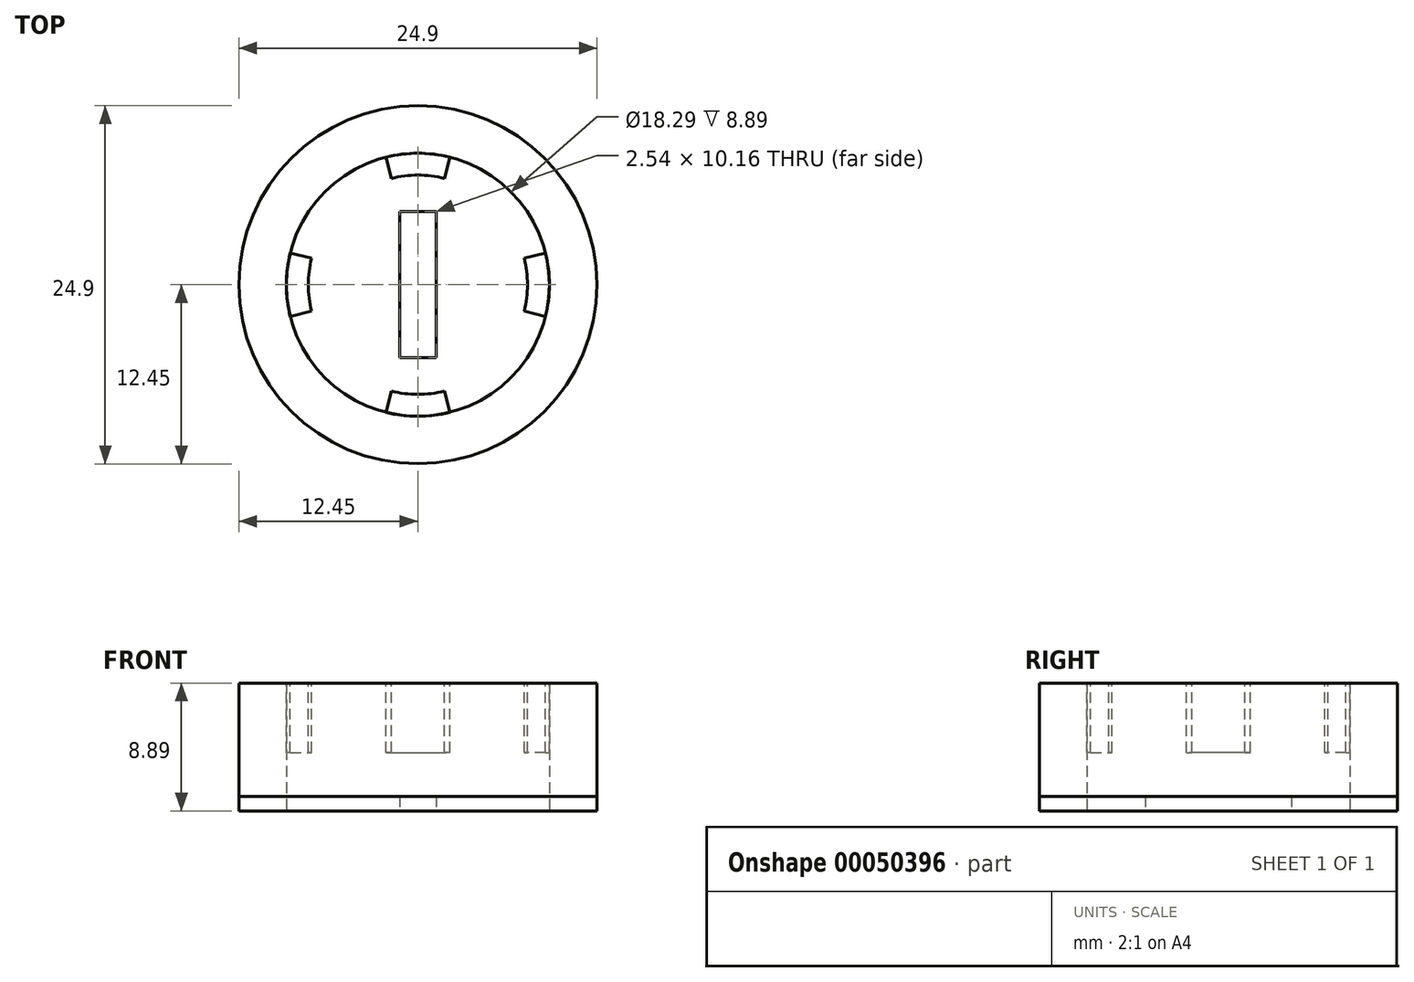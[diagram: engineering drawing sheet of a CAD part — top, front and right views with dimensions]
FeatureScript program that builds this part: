
annotation { "Feature Type Name" : "Feature", "Feature Type Description" : "" }
export const myFeature = defineFeature(function(context is Context, id is Id, definition is map)
    precondition{}
    {
        {
            var Q0;
            Q0=qCreatedBy(makeId("Top.planeOp"),FACE);
            var sketch = newSketch(context, id + "F0", { "sketchPlane" : qUnion([Q0])});
            skCircle(sketch, "E0", {"center": v(0, 0) * mm, "radius": 7.62 * mm});
            skCircle(sketch, "E1", {"center": v(0, 0) * mm, "radius": 12.45 * mm});
            skCircle(sketch, "E2", {"center": v(0, 0) * mm, "radius": 9.14 * mm});
            skLineSegment(sketch, "E3", {"start": v(0, 0) * mm, "end": v(0, 9.14) * mm});
            skLineSegment(sketch, "E4.1.0", {"start": v(0, 0) * mm, "end": v(-2.37, 8.83) * mm});
            skLineSegment(sketch, "E4.2.0", {"start": v(0, 0) * mm, "end": v(-4.57, 7.92) * mm});
            skLineSegment(sketch, "E4.3.0", {"start": v(0, 0) * mm, "end": v(-6.47, 6.47) * mm});
            skLineSegment(sketch, "E4.4.0", {"start": v(0, 0) * mm, "end": v(-7.92, 4.57) * mm});
            skLineSegment(sketch, "E4.5.0", {"start": v(0, 0) * mm, "end": v(-8.83, 2.37) * mm});
            skLineSegment(sketch, "E4.6.0", {"start": v(0, 0) * mm, "end": v(-9.14, 0) * mm});
            skLineSegment(sketch, "E4.7.0", {"start": v(0, 0) * mm, "end": v(-8.83, -2.37) * mm});
            skLineSegment(sketch, "E4.8.0", {"start": v(0, 0) * mm, "end": v(-7.92, -4.57) * mm});
            skLineSegment(sketch, "E4.9.0", {"start": v(0, 0) * mm, "end": v(-6.47, -6.47) * mm});
            skLineSegment(sketch, "E4.10.0", {"start": v(0, 0) * mm, "end": v(-4.57, -7.92) * mm});
            skLineSegment(sketch, "E4.11.0", {"start": v(0, 0) * mm, "end": v(-2.37, -8.83) * mm});
            skLineSegment(sketch, "E4.12.0", {"start": v(0, 0) * mm, "end": v(0, -9.14) * mm});
            skLineSegment(sketch, "E4.13.0", {"start": v(0, 0) * mm, "end": v(2.37, -8.83) * mm});
            skLineSegment(sketch, "E4.14.0", {"start": v(0, 0) * mm, "end": v(4.57, -7.92) * mm});
            skLineSegment(sketch, "E4.15.0", {"start": v(0, 0) * mm, "end": v(6.47, -6.47) * mm});
            skLineSegment(sketch, "E4.16.0", {"start": v(0, 0) * mm, "end": v(7.92, -4.57) * mm});
            skLineSegment(sketch, "E4.17.0", {"start": v(0, 0) * mm, "end": v(8.83, -2.37) * mm});
            skLineSegment(sketch, "E4.18.0", {"start": v(0, 0) * mm, "end": v(9.14, 0) * mm});
            skLineSegment(sketch, "E4.19.0", {"start": v(0, 0) * mm, "end": v(8.83, 2.37) * mm});
            skLineSegment(sketch, "E4.20.0", {"start": v(0, 0) * mm, "end": v(7.92, 4.57) * mm});
            skLineSegment(sketch, "E4.21.0", {"start": v(0, 0) * mm, "end": v(6.47, 6.47) * mm});
            skLineSegment(sketch, "E4.22.0", {"start": v(0, 0) * mm, "end": v(4.57, 7.92) * mm});
            skLineSegment(sketch, "E4.23.0", {"start": v(0, 0) * mm, "end": v(2.37, 8.83) * mm});
            skLineSegment(sketch, "E5", {"start": v(0, 0) * mm, "end": v(2.21, 8.87) * mm});
            skLineSegment(sketch, "E6", {"start": v(0, 0) * mm, "end": v(-2.21, 8.87) * mm});
            skLineSegment(sketch, "E7.1.0", {"start": v(0, 0) * mm, "end": v(-8.87, -2.21) * mm});
            skLineSegment(sketch, "E7.1.1", {"start": v(0, 0) * mm, "end": v(-8.87, 2.21) * mm});
            skLineSegment(sketch, "E7.2.0", {"start": v(0, 0) * mm, "end": v(2.21, -8.87) * mm});
            skLineSegment(sketch, "E7.2.1", {"start": v(0, 0) * mm, "end": v(-2.21, -8.87) * mm});
            skLineSegment(sketch, "E7.3.0", {"start": v(0, 0) * mm, "end": v(8.87, 2.21) * mm});
            skLineSegment(sketch, "E7.3.1", {"start": v(0, 0) * mm, "end": v(8.87, -2.21) * mm});
            skSolve(sketch);
        }
        {
            var Q0;
            Q0=makeQuery(id+"F0.imprint","IMPRINT",FACE,{"disambiguationData":[TD([[makeQuery(id+"F0.imprint","IMPRINT",EDGE,{"derivedFrom":sQuery(id+"F0.wireOp",EDGE,"E1")}),1.0]])]});
            extrude(context, id + "F1", {"entities" : qUnion([Q0]), "depth" : 8.9 * mm});
        }
        {
            var Q0;
            Q0=makeQuery(id+"F1.opExtrude","CAP_FACE",FACE,{"disambiguationData":[OSD([sQuery(id+"F0.wireOp",EDGE,"E1"),sQuery(id+"F0.wireOp",EDGE,"E2")])],"isStart":false});
            var sketch = newSketch(context, id + "F2", { "sketchPlane" : qUnion([Q0])});
            skLineSegment(sketch, "E8.0.0", {"start": v(-9.14, 0) * mm, "end": v(-7.62, 0) * mm});
            skArc(sketch, "E8.0.1", {"start": v(-7.62, 0) * mm, "mid": v(-7.56, 0.93) * mm, "end": v(-7.4, 1.84) * mm});
            skLineSegment(sketch, "E8.0.2", {"start": v(-7.4, 1.84) * mm, "end": v(-8.87, 2.21) * mm});
            skArc(sketch, "E8.0.3", {"start": v(-8.87, 2.21) * mm, "mid": v(-9.08, 1.11) * mm, "end": v(-9.14, 0) * mm});
            skArc(sketch, "E9.0.0", {"start": v(-7.4, -1.84) * mm, "mid": v(-7.56, -0.93) * mm, "end": v(-7.62, 0) * mm});
            skLineSegment(sketch, "E9.0.1", {"start": v(-7.62, 0) * mm, "end": v(-9.14, 0) * mm});
            skArc(sketch, "E9.0.2", {"start": v(-9.14, 0) * mm, "mid": v(-9.08, -1.11) * mm, "end": v(-8.87, -2.21) * mm});
            skLineSegment(sketch, "E9.0.3", {"start": v(-8.87, -2.21) * mm, "end": v(-7.4, -1.84) * mm});
            skLineSegment(sketch, "E10.0.0", {"start": v(0, -9.14) * mm, "end": v(0, -7.62) * mm});
            skArc(sketch, "E10.0.1", {"start": v(0, -7.62) * mm, "mid": v(-0.93, -7.56) * mm, "end": v(-1.84, -7.4) * mm});
            skLineSegment(sketch, "E10.0.2", {"start": v(-1.84, -7.4) * mm, "end": v(-2.21, -8.87) * mm});
            skArc(sketch, "E10.0.3", {"start": v(-2.21, -8.87) * mm, "mid": v(-1.11, -9.08) * mm, "end": v(0, -9.14) * mm});
            skArc(sketch, "E11.0.0", {"start": v(1.84, -7.4) * mm, "mid": v(0.93, -7.56) * mm, "end": v(0, -7.62) * mm});
            skLineSegment(sketch, "E11.0.1", {"start": v(0, -7.62) * mm, "end": v(0, -9.14) * mm});
            skArc(sketch, "E11.0.2", {"start": v(0, -9.14) * mm, "mid": v(1.11, -9.08) * mm, "end": v(2.21, -8.87) * mm});
            skLineSegment(sketch, "E11.0.3", {"start": v(2.21, -8.87) * mm, "end": v(1.84, -7.4) * mm});
            skLineSegment(sketch, "E12.0.0", {"start": v(9.14, 0) * mm, "end": v(7.62, 0) * mm});
            skArc(sketch, "E12.0.1", {"start": v(7.62, 0) * mm, "mid": v(7.56, -0.93) * mm, "end": v(7.4, -1.84) * mm});
            skLineSegment(sketch, "E12.0.2", {"start": v(7.4, -1.84) * mm, "end": v(8.87, -2.21) * mm});
            skArc(sketch, "E12.0.3", {"start": v(8.87, -2.21) * mm, "mid": v(9.08, -1.11) * mm, "end": v(9.14, 0) * mm});
            skArc(sketch, "E13.0.0", {"start": v(7.4, 1.84) * mm, "mid": v(7.56, 0.93) * mm, "end": v(7.62, 0) * mm});
            skLineSegment(sketch, "E13.0.1", {"start": v(7.62, 0) * mm, "end": v(9.14, 0) * mm});
            skArc(sketch, "E13.0.2", {"start": v(9.14, 0) * mm, "mid": v(9.08, 1.11) * mm, "end": v(8.87, 2.21) * mm});
            skLineSegment(sketch, "E13.0.3", {"start": v(8.87, 2.21) * mm, "end": v(7.4, 1.84) * mm});
            skLineSegment(sketch, "E14.0.0", {"start": v(0, 9.14) * mm, "end": v(0, 7.62) * mm});
            skArc(sketch, "E14.0.1", {"start": v(0, 7.62) * mm, "mid": v(0.93, 7.56) * mm, "end": v(1.84, 7.4) * mm});
            skLineSegment(sketch, "E14.0.2", {"start": v(1.84, 7.4) * mm, "end": v(2.21, 8.87) * mm});
            skArc(sketch, "E14.0.3", {"start": v(2.21, 8.87) * mm, "mid": v(1.11, 9.08) * mm, "end": v(0, 9.14) * mm});
            skArc(sketch, "E15.0.0", {"start": v(-1.84, 7.4) * mm, "mid": v(-0.93, 7.56) * mm, "end": v(0, 7.62) * mm});
            skLineSegment(sketch, "E15.0.1", {"start": v(0, 7.62) * mm, "end": v(0, 9.14) * mm});
            skArc(sketch, "E15.0.2", {"start": v(0, 9.14) * mm, "mid": v(-1.11, 9.08) * mm, "end": v(-2.21, 8.87) * mm});
            skLineSegment(sketch, "E15.0.3", {"start": v(-2.21, 8.87) * mm, "end": v(-1.84, 7.4) * mm});
            skSolve(sketch);
        }
        {
            var Q0;
            Q0 = qSketchRegion(id + "F2", true);
            extrude(context, id + "F3", {"entities" : qUnion([Q0]), "oppositeDirection" : true, "depth" : 4.83 * mm});
        }
        {
            var Q0;
            Q0=makeQuery(id+"F0.imprint","IMPRINT",FACE,{"disambiguationData":[TD([[makeQuery(id+"F0.imprint","IMPRINT",EDGE,{"derivedFrom":sQuery(id+"F0.wireOp",EDGE,"E1")}),1.0]])]});
            var sketch = newSketch(context, id + "F4", { "sketchPlane" : qUnion([Q0])});
            skCircle(sketch, "E16.0", {"center": v(0, 0) * mm, "radius": 12.45 * mm});
            skSolve(sketch);
        }
        {
            var Q0;
            Q0 = qSketchRegion(id + "F4", true);
            extrude(context, id + "F5", {"entities" : qUnion([Q0]), "depth" : 1.02 * mm});
        }
        {
            var Q0;
            Q0=makeQuery(id+"F0.imprint","IMPRINT",FACE,{"disambiguationData":[TD([[makeQuery(id+"F0.imprint","IMPRINT",EDGE,{"derivedFrom":sQuery(id+"F0.wireOp",EDGE,"E1")}),1.0]])]});
            var sketch = newSketch(context, id + "F6", { "sketchPlane" : qUnion([Q0])});
            skLineSegment(sketch, "E17.rect.bottom", {"start": v(1.27, 5.08) * mm, "end": v(-1.27, 5.08) * mm});
            skLineSegment(sketch, "E17.rect.top", {"start": v(1.27, -5.08) * mm, "end": v(-1.27, -5.08) * mm});
            skLineSegment(sketch, "E17.rect.left", {"start": v(1.27, 5.08) * mm, "end": v(1.27, -5.08) * mm});
            skLineSegment(sketch, "E17.rect.right", {"start": v(-1.27, 5.08) * mm, "end": v(-1.27, -5.08) * mm});
            skPoint(sketch, "E17.rect.middle", {"position": v(0, 0) * mm});
            skSolve(sketch);
        }
        {
            var Q0;
            Q0 = qSketchRegion(id + "F6", true);
            extrude(context, id + "F7", {"entities" : qUnion([Q0]), "operationType" : NewBodyOperationType.REMOVE, "depth" : 2.54 * mm});
        }
    });
